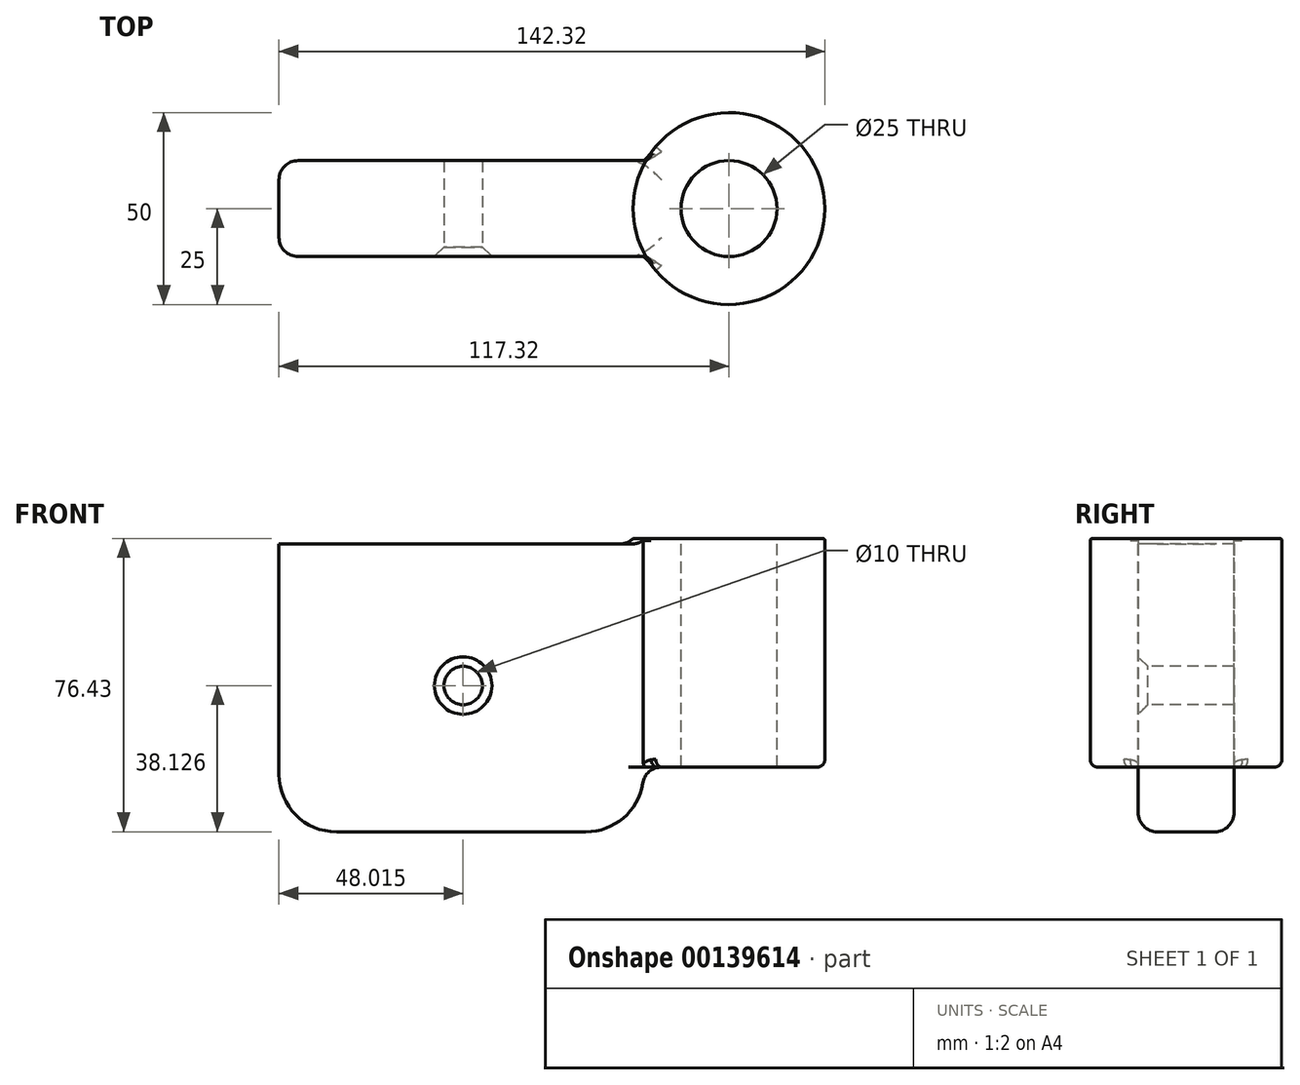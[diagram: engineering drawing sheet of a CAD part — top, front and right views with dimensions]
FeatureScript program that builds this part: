
annotation { "Feature Type Name" : "Feature", "Feature Type Description" : "" }
export const myFeature = defineFeature(function(context is Context, id is Id, definition is map)
    precondition{}
    {
        {
            var Q0;
            Q0=qCreatedBy(makeId("Front.planeOp"),FACE);
            var sketch = newSketch(context, id + "F0", { "sketchPlane" : qUnion([Q0])});
            skLineSegment(sketch, "E0.bottom", {"start": v(-47.5, 37.5) * mm, "end": v(47.5, 37.5) * mm});
            skLineSegment(sketch, "E0.top", {"start": v(-47.5, -37.5) * mm, "end": v(47.5, -37.5) * mm});
            skLineSegment(sketch, "E0.left", {"start": v(-47.5, 37.5) * mm, "end": v(-47.5, -37.5) * mm});
            skLineSegment(sketch, "E0.right", {"start": v(47.5, 37.5) * mm, "end": v(47.5, -37.5) * mm});
            skLineSegment(sketch, "E1", {"start": v(0, 0) * mm, "end": v(0, 23.98) * mm, "construction": true});
            skLineSegment(sketch, "E2", {"start": v(0, 0) * mm, "end": v(-22.05, 0) * mm, "construction": true});
            skSolve(sketch);
        }
        {
            var Q0;
            Q0 = qSketchRegion(id + "F0", true);
            extrude(context, id + "F1", {"entities" : qUnion([Q0]), "endBound" : BoundingType.SYMMETRIC, "depth" : 25 * mm});
        }
        {
            var Q0;
            Q0=makeQuery(id+"F1.opExtrude","CAP_FACE",FACE,{"disambiguationData":[OSD([sQuery(id+"F0.wireOp",EDGE,"E0.bottom"),sQuery(id+"F0.wireOp",EDGE,"E0.top"),sQuery(id+"F0.wireOp",EDGE,"E0.left"),sQuery(id+"F0.wireOp",EDGE,"E0.right")])],"isStart":false});
            var sketch = newSketch(context, id + "F2", { "sketchPlane" : qUnion([Q0])});
            skPoint(sketch, "E3", {"position": v(0.51, 0.63) * mm});
            skSolve(sketch);
        }
        {
            var Q0;
            Q0=sQuery(id+"F2.wireOp",VERTEX,"E3");
            var Q1;
            Q1=makeQuery(id+"F1.opExtrude","SWEPT_BODY",BODY,{"disambiguationData":[OSD([sQuery(id+"F0.wireOp",EDGE,"E0.bottom"),sQuery(id+"F0.wireOp",EDGE,"E0.top"),sQuery(id+"F0.wireOp",EDGE,"E0.left"),sQuery(id+"F0.wireOp",EDGE,"E0.right")])]});
            hole(context, id + "F3", {"style" : HoleStyle.C_SINK, "endStyle" : HoleEndStyle.THROUGH, "holeDiameter" : 10 * mm, "cSinkDiameter" : 15 * mm, "cSinkAngle" : 90 * degree, "locations" : qUnion([Q0]), "scope" : qUnion([Q1]), "isTappedThrough" : true});
        }
        {
            var Q0;
            Q0=makeQuery(id+"F1.opExtrude","SWEPT_EDGE",EDGE,{"disambiguationData":[OSD([sQuery(id+"F0.wireOp",EDGE,"E0.top"),sQuery(id+"F0.wireOp",EDGE,"E0.right")])]});
            var Q1;
            Q1=makeQuery(id+"F1.opExtrude","SWEPT_EDGE",EDGE,{"disambiguationData":[OSD([sQuery(id+"F0.wireOp",EDGE,"E0.top"),sQuery(id+"F0.wireOp",EDGE,"E0.left")])]});
            fillet(context, id + "F4", {"entities" : qUnion([Q0, Q1]), "radius" : 15 * mm, "tangentPropagation" : true, "allowEdgeOverflow" : false});
        }
        {
            var Q0;
            Q0=qCreatedBy(makeId("Front.planeOp"),FACE);
            var sketch = newSketch(context, id + "F5", { "sketchPlane" : qUnion([Q0])});
            skLineSegment(sketch, "E4", {"start": v(82.32, 38.93) * mm, "end": v(94.82, 38.93) * mm});
            skLineSegment(sketch, "E5", {"start": v(94.82, 38.93) * mm, "end": v(94.82, -20.63) * mm});
            skLineSegment(sketch, "E6", {"start": v(94.82, -20.63) * mm, "end": v(82.32, -20.63) * mm});
            skLineSegment(sketch, "E7", {"start": v(69.82, 38.93) * mm, "end": v(69.82, -20.63) * mm, "construction": true});
            skLineSegment(sketch, "E8", {"start": v(82.32, 38.93) * mm, "end": v(82.32, -20.63) * mm});
            skSolve(sketch);
        }
        {
            var Q0;
            Q0 = qSketchRegion(id + "F5", true);
            var Q1;
            Q1=sQuery(id+"F5.wireOp",EDGE,"E7");
            revolve(context, id + "F6", {"operationType" : NewBodyOperationType.ADD, "entities" : qUnion([Q0]), "axis" : qUnion([Q1]), "revolveType" : RevolveType.FULL});
        }
        {
            var Q0;
            Q0=makeQuery(id+"F6.boolean.opBoolean","INTERSECT",EDGE,{"disambiguationData":[OD(1.0)],"derivedFrom":[makeQuery(id+"F1.opExtrude","SWEPT_FACE",FACE,{"disambiguationData":[OSD([sQuery(id+"F0.wireOp",EDGE,"E0.right")])]}),makeQuery(id+"F6.opRevolve","SWEPT_FACE",FACE,{"disambiguationData":[OSD([sQuery(id+"F5.wireOp",EDGE,"E5")])]})]});
            var Q1;
            Q1=makeQuery(id+"FKMeXUtmhrkZppJ_1.1.F6.boolean.opBoolean","INTERSECT",EDGE,{"disambiguationData":[OD(1.0)],"derivedFrom":[makeQuery(id+"F1.opExtrude","SWEPT_FACE",FACE,{"disambiguationData":[OSD([sQuery(id+"F0.wireOp",EDGE,"E0.left")])]}),makeQuery(id+"FKMeXUtmhrkZppJ_1.1.F6.opRevolve","SWEPT_FACE",FACE,{"disambiguationData":[OSD([sQuery(id+"F5.wireOp",EDGE,"E5")])]})]});
            var Q2;
            Q2=makeQuery(id+"FKMeXUtmhrkZppJ_1.1.F6.boolean.opBoolean","INTERSECT",EDGE,{"disambiguationData":[OD(0.0)],"derivedFrom":[makeQuery(id+"F1.opExtrude","SWEPT_FACE",FACE,{"disambiguationData":[OSD([sQuery(id+"F0.wireOp",EDGE,"E0.left")])]}),makeQuery(id+"FKMeXUtmhrkZppJ_1.1.F6.opRevolve","SWEPT_FACE",FACE,{"disambiguationData":[OSD([sQuery(id+"F5.wireOp",EDGE,"E5")])]})]});
            var Q3;
            Q3=makeQuery(id+"F6.boolean.opBoolean","INTERSECT",EDGE,{"disambiguationData":[OD(0.0)],"derivedFrom":[makeQuery(id+"F1.opExtrude","SWEPT_FACE",FACE,{"disambiguationData":[OSD([sQuery(id+"F0.wireOp",EDGE,"E0.right")])]}),makeQuery(id+"F6.opRevolve","SWEPT_FACE",FACE,{"disambiguationData":[OSD([sQuery(id+"F5.wireOp",EDGE,"E5")])]})]});
            fillet(context, id + "F7", {"entities" : qUnion([Q0, Q1, Q2, Q3]), "radius" : 10 * mm, "rho" : 0.5, "crossSection" : FilletCrossSection.CONIC, "allowEdgeOverflow" : false});
        }
        {
            var Q0;
            Q0=makeQuery(id+"FKMeXUtmhrkZppJ_1.1.F6.boolean.opBoolean","INTERSECT",EDGE,{"derivedFrom":[makeQuery(id+"F1.opExtrude","SWEPT_FACE",FACE,{"disambiguationData":[OSD([sQuery(id+"F0.wireOp",EDGE,"E0.left")])]}),makeQuery(id+"FKMeXUtmhrkZppJ_1.1.F6.opRevolve","SWEPT_FACE",FACE,{"disambiguationData":[OSD([sQuery(id+"F5.wireOp",EDGE,"E6")])]})]});
            var Q1;
            Q1=makeQuery(id+"F6.boolean.opBoolean","INTERSECT",EDGE,{"derivedFrom":[makeQuery(id+"F1.opExtrude","SWEPT_FACE",FACE,{"disambiguationData":[OSD([sQuery(id+"F0.wireOp",EDGE,"E0.right")])]}),makeQuery(id+"F6.opRevolve","SWEPT_FACE",FACE,{"disambiguationData":[OSD([sQuery(id+"F5.wireOp",EDGE,"E6")])]})]});
            var Q2;
            Q2=makeQuery(id+"F6.boolean.opBoolean","INTERSECT",EDGE,{"derivedFrom":[makeQuery(id+"F1.opExtrude","SWEPT_FACE",FACE,{"disambiguationData":[OSD([sQuery(id+"F0.wireOp",EDGE,"E0.bottom")])]}),makeQuery(id+"F6.opRevolve","SWEPT_FACE",FACE,{"disambiguationData":[OSD([sQuery(id+"F5.wireOp",EDGE,"E5")])]})]});
            var Q3;
            Q3=makeQuery(id+"FKMeXUtmhrkZppJ_1.1.F6.boolean.opBoolean","INTERSECT",EDGE,{"derivedFrom":[makeQuery(id+"F1.opExtrude","SWEPT_FACE",FACE,{"disambiguationData":[OSD([sQuery(id+"F0.wireOp",EDGE,"E0.bottom")])]}),makeQuery(id+"FKMeXUtmhrkZppJ_1.1.F6.opRevolve","SWEPT_FACE",FACE,{"disambiguationData":[OSD([sQuery(id+"F5.wireOp",EDGE,"E5")])]})]});
            fillet(context, id + "F8", {"entities" : qUnion([Q0, Q1, Q2, Q3]), "radius" : 5 * mm, "tangentPropagation" : true, "allowEdgeOverflow" : false});
        }
        {
            var Q0;
            Q0=makeQuery(id+"FKMeXUtmhrkZppJ_1.1.F6.opRevolve","SWEPT_EDGE",EDGE,{"disambiguationData":[OSD([sQuery(id+"F5.wireOp",EDGE,"E5"),sQuery(id+"F5.wireOp",EDGE,"E6")])]});
            var Q1;
            Q1=makeQuery(id+"F6.opRevolve","SWEPT_EDGE",EDGE,{"disambiguationData":[OSD([sQuery(id+"F5.wireOp",EDGE,"E5"),sQuery(id+"F5.wireOp",EDGE,"E6")])]});
            fillet(context, id + "F9", {"entities" : qUnion([Q0, Q1]), "radius" : 2 * mm, "tangentPropagation" : true, "allowEdgeOverflow" : false});
        }
        {
            var Q0;
            Q0=makeQuery(id+"FKMeXUtmhrkZppJ_1.1.F6.opRevolve","SWEPT_EDGE",EDGE,{"disambiguationData":[OSD([sQuery(id+"F5.wireOp",EDGE,"E4"),sQuery(id+"F5.wireOp",EDGE,"E5")])]});
            var Q1;
            Q1=makeQuery(id+"F6.opRevolve","SWEPT_EDGE",EDGE,{"disambiguationData":[OSD([sQuery(id+"F5.wireOp",EDGE,"E4"),sQuery(id+"F5.wireOp",EDGE,"E5")])]});
            fillet(context, id + "F10", {"entities" : qUnion([Q0, Q1]), "radius" : 0.5 * mm, "tangentPropagation" : true, "allowEdgeOverflow" : false});
        }
        {
            var Q0;
            Q0=makeQuery(id+"F1.opExtrude","CAP_EDGE",EDGE,{"disambiguationData":[OSD([sQuery(id+"F0.wireOp",EDGE,"E0.top")])],"isStart":false});
            var Q1;
            Q1=makeQuery(id+"F1.opExtrude","CAP_EDGE",EDGE,{"disambiguationData":[OSD([sQuery(id+"F0.wireOp",EDGE,"E0.top")])],"isStart":true});
            fillet(context, id + "F11", {"entities" : qUnion([Q0, Q1]), "radius" : 5 * mm, "tangentPropagation" : true, "allowEdgeOverflow" : false});
        }
    });
